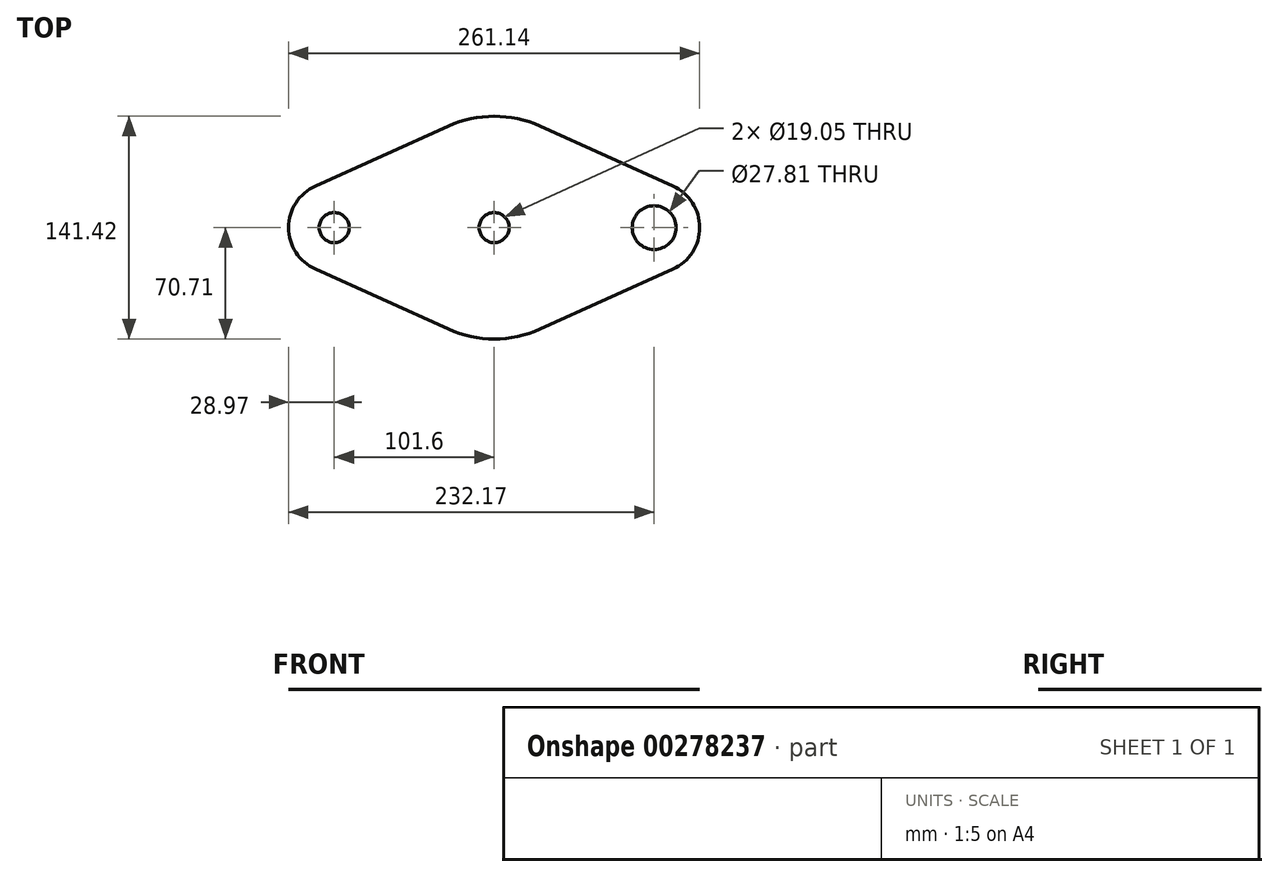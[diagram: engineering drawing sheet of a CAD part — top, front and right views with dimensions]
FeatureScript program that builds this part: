
annotation { "Feature Type Name" : "Feature", "Feature Type Description" : "" }
export const myFeature = defineFeature(function(context is Context, id is Id, definition is map)
    precondition{}
    {
        {
            var Q0;
            Q0=qCreatedBy(makeId("Top.planeOp"),FACE);
            var sketch = newSketch(context, id + "F0", { "sketchPlane" : qUnion([Q0])});
            skCircle(sketch, "E0", {"center": v(0, 0) * mm, "radius": 64.77 * mm});
            skCircle(sketch, "E1", {"center": v(0, 0) * mm, "radius": 70.7 * mm});
            skLineSegment(sketch, "E2", {"start": v(0, 0) * mm, "end": v(-101.6, 0) * mm});
            skCircle(sketch, "E3", {"center": v(-101.6, 0) * mm, "radius": 9.53 * mm});
            skCircle(sketch, "E4", {"center": v(-101.6, 0) * mm, "radius": 13.9 * mm});
            skLineSegment(sketch, "E5.MirrorCS", {"start": v(0, 0) * mm, "end": v(101.6, 0) * mm});
            skCircle(sketch, "E6.MirrorC", {"center": v(101.6, 0) * mm, "radius": 13.9 * mm});
            skCircle(sketch, "E7", {"center": v(-101.6, 0) * mm, "radius": 28.97 * mm});
            skCircle(sketch, "E8.MirrorC", {"center": v(101.6, 0) * mm, "radius": 28.97 * mm});
            skLineSegment(sketch, "E9", {"start": v(-113.5, 26.41) * mm, "end": v(-29.05, 64.46) * mm});
            skLineSegment(sketch, "E10", {"start": v(-113.5, -26.41) * mm, "end": v(-29.05, -64.46) * mm});
            skLineSegment(sketch, "E11.MirrorCS", {"start": v(113.5, 26.41) * mm, "end": v(29.05, 64.46) * mm});
            skLineSegment(sketch, "E12.MirrorCS", {"start": v(113.5, -26.41) * mm, "end": v(29.05, -64.46) * mm});
            skCircle(sketch, "E13", {"center": v(0, 0) * mm, "radius": 9.53 * mm});
            skCircle(sketch, "E14", {"center": v(101.6, 0) * mm, "radius": 9.53 * mm});
            skSolve(sketch);
        }
        {
            var Q0;
            Q0=qSketchRegion(id+"F0",true);
            var Q1;
            {var subQ0=sQuery(id+"F0.wireOp",EDGE,"E13");var subQ1=sQuery(id+"F0.wireOp",EDGE,"E2");var subQ2=makeQuery(id+"F0.imprint","INTERSECT",VERTEX,{"derivedFrom":[subQ1,subQ0]});Q1=makeQuery(id+"F0.imprint","IMPRINT",FACE,{"disambiguationData":[TD([[makeQuery(id+"F0.imprint","IMPRINT",EDGE,{"disambiguationData":[TD([[subQ2,-1.0]])],"derivedFrom":subQ1}),1.0]])]});}
            var Q2;
            {var subQ0=sQuery(id+"F0.wireOp",EDGE,"E13");var subQ1=sQuery(id+"F0.wireOp",EDGE,"E2");var subQ2=makeQuery(id+"F0.imprint","INTERSECT",VERTEX,{"derivedFrom":[subQ1,subQ0]});Q2=makeQuery(id+"F0.imprint","IMPRINT",FACE,{"disambiguationData":[TD([[makeQuery(id+"F0.imprint","IMPRINT",EDGE,{"disambiguationData":[TD([[subQ2,-1.0]])],"derivedFrom":subQ1}),-1.0]])]});}
            var Q3;
            Q3=makeQuery(id+"F0.imprint","IMPRINT",FACE,{"disambiguationData":[TD([[makeQuery(id+"F0.imprint","IMPRINT",EDGE,{"derivedFrom":sQuery(id+"F0.wireOp",EDGE,"E6.MirrorC")}),-1.0]])]});
            var Q4;
            Q4=makeQuery(id+"F0.imprint","IMPRINT",FACE,{"disambiguationData":[TD([[makeQuery(id+"F0.imprint","IMPRINT",EDGE,{"derivedFrom":sQuery(id+"F0.wireOp",EDGE,"E3")}),-1.0]])]});
            extrude(context, id + "F1", {"entities" : qUnion([Q0, Q1, Q2, Q3, Q4]), "depth" : 1 / 203.2 * mm});
        }
    });
